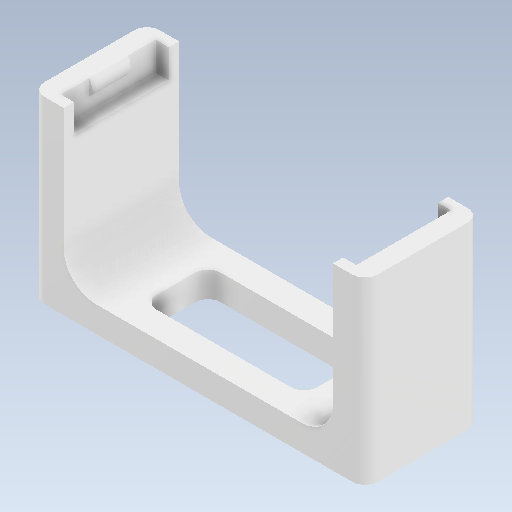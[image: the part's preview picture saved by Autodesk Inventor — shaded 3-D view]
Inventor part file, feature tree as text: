
AUTODESK INVENTOR PART (.ipt)
format: ipt  version: 2021 (Build 250183000, 183)  size: 243,712 bytes
history: mixed  units: in
note: dims shown in document units (in); Inventor stores cm internally (conversion verified against a paired STEP export)
features: extrude x6, sketch x6, projected_geometry x6, fillet x2, mirror x1, imported_body x1
ambient origin geometry x8: Origin, YZ Plane, XZ Plane, XY Plane, X Axis, Y Axis, Z Axis, Center Point
bodies: Solid1 (imported_parasolid)
feature tree (22):
  extrude  "Extrusion1"  Depth=0.0984in
  extrude  "Extrusion5"  Depth=0.2362in
  extrude  "Extrusion2"  Depth=0.3937in TaperAngle=0.0deg
  mirror  "Mirror1"
  extrude  "Extrusion3"  Depth=0.1969in
  extrude  "Extrusion4"  Depth=0.3937in
  fillet  "Fillet4"  Radius=0.3937in
  extrude  "Extrusion6"  Depth=0.2362in
  sketch  "Sketch1"  dims[d0=0.0984in d1=0.0in d3=0.0984in]
  projected_geometry  "Projected Loop1"
  projected_geometry  "Projected Loop2"
  sketch  "Sketch2"  dims[d4=0.2362in d5=0.0in d7=0.0394in]
  projected_geometry  "Projected Loop3"
  sketch  "Sketch3"  dims[d8=0.0394in d9=0.3937in d10=0.7874in d11=0.0in d12=0.0in]
  sketch  "Sketch4"  dims[d14=0.0394in d15=0.0in d16=0.1969in]
  projected_geometry  "Projected Loop4"
  sketch  "Sketch6"  dims[d17=0.5827in d18=0.5551in d19=0.3937in d20=0.0in]
  sketch  "Sketch7"  dims[d22=0.0197in d23=0.0in d24=0.0197in d25=0.2362in]
  projected_geometry  "Projected Loop5"
  projected_geometry  "Projected Loop6"
  fillet  "Fillet2"  Radius=0.2362in
  imported_body  NMx_Import_Brep_tag  [imported B-rep: ~38 faces, bbox_mm=[52.0, 28.0, 18.0]]
